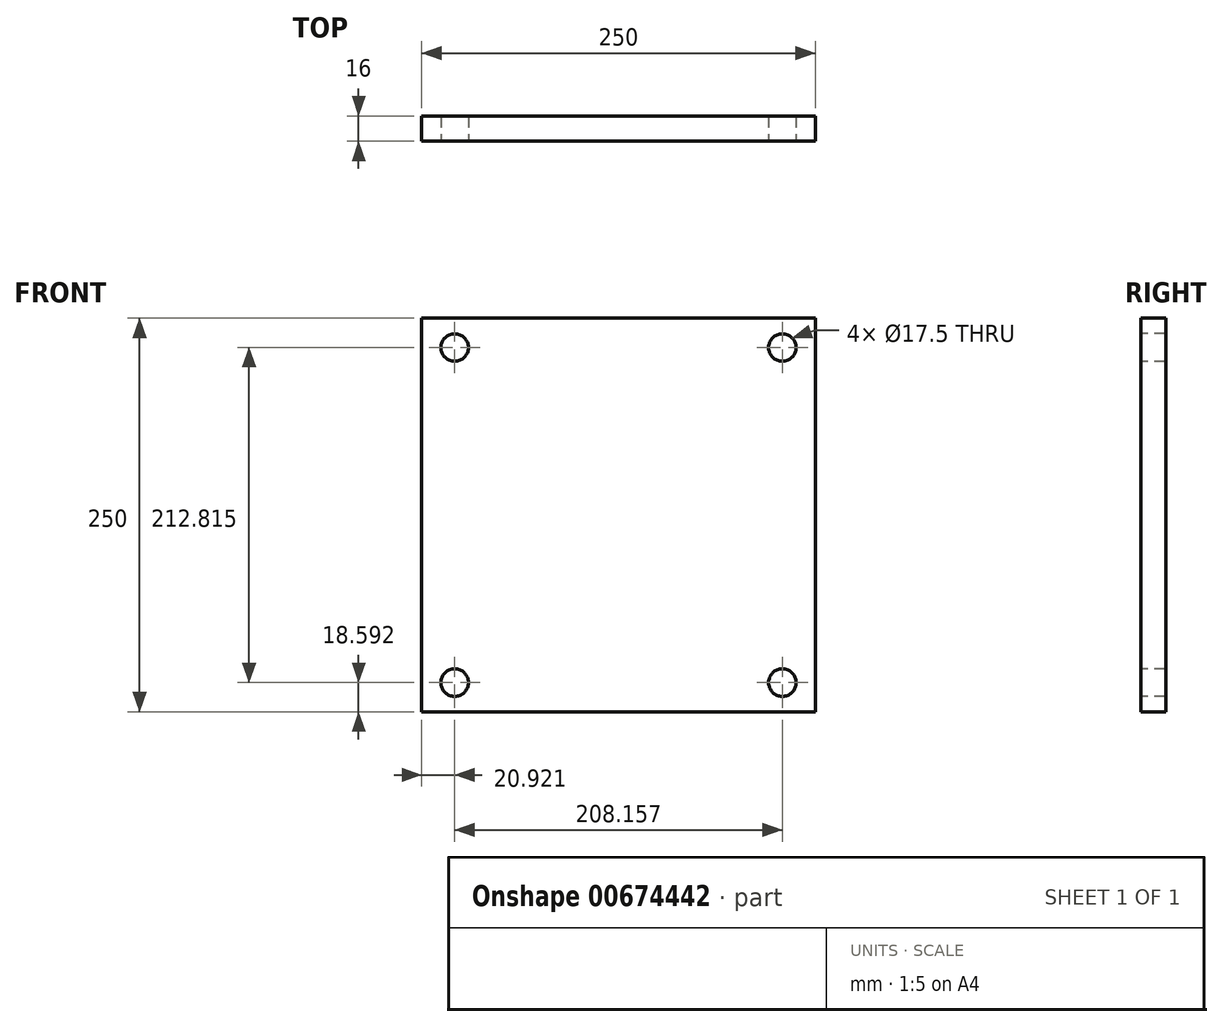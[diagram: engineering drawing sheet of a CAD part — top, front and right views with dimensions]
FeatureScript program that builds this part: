
annotation { "Feature Type Name" : "Feature", "Feature Type Description" : "" }
export const myFeature = defineFeature(function(context is Context, id is Id, definition is map)
    precondition{}
    {
        {
            var Q0;
            Q0=qCreatedBy(makeId("Front.planeOp"),FACE);
            var sketch = newSketch(context, id + "F0", { "sketchPlane" : qUnion([Q0])});
            skLineSegment(sketch, "E0.bottom", {"start": v(0, 0) * mm, "end": v(250, 0) * mm});
            skLineSegment(sketch, "E0.top", {"start": v(0, 250) * mm, "end": v(250, 250) * mm});
            skLineSegment(sketch, "E0.left", {"start": v(0, 0) * mm, "end": v(0, 250) * mm});
            skLineSegment(sketch, "E0.right", {"start": v(250, 0) * mm, "end": v(250, 250) * mm});
            skSolve(sketch);
        }
        {
            var Q0;
            Q0 = qSketchRegion(id + "F0", true);
            extrude(context, id + "F1", {"entities" : qUnion([Q0]), "depth" : 16 * mm, "offsetDistance" : 25 * mm});
        }
        {
            var Q0;
            Q0=makeQuery(id+"F1.opExtrude","CAP_FACE",FACE,{"disambiguationData":[OSD([sQuery(id+"F0.wireOp",EDGE,"E0.bottom"),sQuery(id+"F0.wireOp",EDGE,"E0.top"),sQuery(id+"F0.wireOp",EDGE,"E0.left"),sQuery(id+"F0.wireOp",EDGE,"E0.right")])],"isStart":false});
            var sketch = newSketch(context, id + "F2", { "sketchPlane" : qUnion([Q0])});
            skPoint(sketch, "E1", {"position": v(20.92, 231.4) * mm});
            skLineSegment(sketch, "E2", {"start": v(125, 250) * mm, "end": v(125, 0) * mm, "construction": true});
            skLineSegment(sketch, "E3", {"start": v(0, 125) * mm, "end": v(250, 125) * mm, "construction": true});
            skPoint(sketch, "E4.MirrorP", {"position": v(229.08, 231.4) * mm});
            skPoint(sketch, "E5.MirrorP", {"position": v(20.92, 18.6) * mm});
            skPoint(sketch, "E6.MirrorP", {"position": v(229.08, 18.6) * mm});
            skSolve(sketch);
        }
        {
            var Q0;
            Q0=sQuery(id+"F2.wireOp",VERTEX,"E1");
            var Q1;
            Q1=sQuery(id+"F2.wireOp",VERTEX,"E5.MirrorP");
            var Q2;
            Q2=sQuery(id+"F2.wireOp",VERTEX,"E6.MirrorP");
            var Q3;
            Q3=sQuery(id+"F2.wireOp",VERTEX,"E4.MirrorP");
            var Q4;
            Q4=makeQuery(id+"F1.opExtrude","SWEPT_BODY",BODY,{"disambiguationData":[OSD([sQuery(id+"F0.wireOp",EDGE,"E0.bottom"),sQuery(id+"F0.wireOp",EDGE,"E0.top"),sQuery(id+"F0.wireOp",EDGE,"E0.left"),sQuery(id+"F0.wireOp",EDGE,"E0.right")])]});
            hole(context, id + "F3", {"style" : HoleStyle.SIMPLE, "endStyle" : HoleEndStyle.THROUGH, "standardTappedOrClearance" : lookupTablePath({ "standard" : "ISO", "fit" : "Normal", "size" : "M16", "type" : "Clearance" }), "standardBlindInLast" : lookupTablePath({ "fit" : "Standard", "standard" : "ISO", "size" : "M16", "type" : "Clearance" }), "holeDiameter" : 17.5 * mm, "majorDiameter" : 16 * mm, "isTappedThrough" : true, "tappedDepth" : 12 * mm, "tapClearance" : 3, "locations" : qUnion([Q0, Q1, Q2, Q3]), "scope" : qUnion([Q4])});
        }
    });
